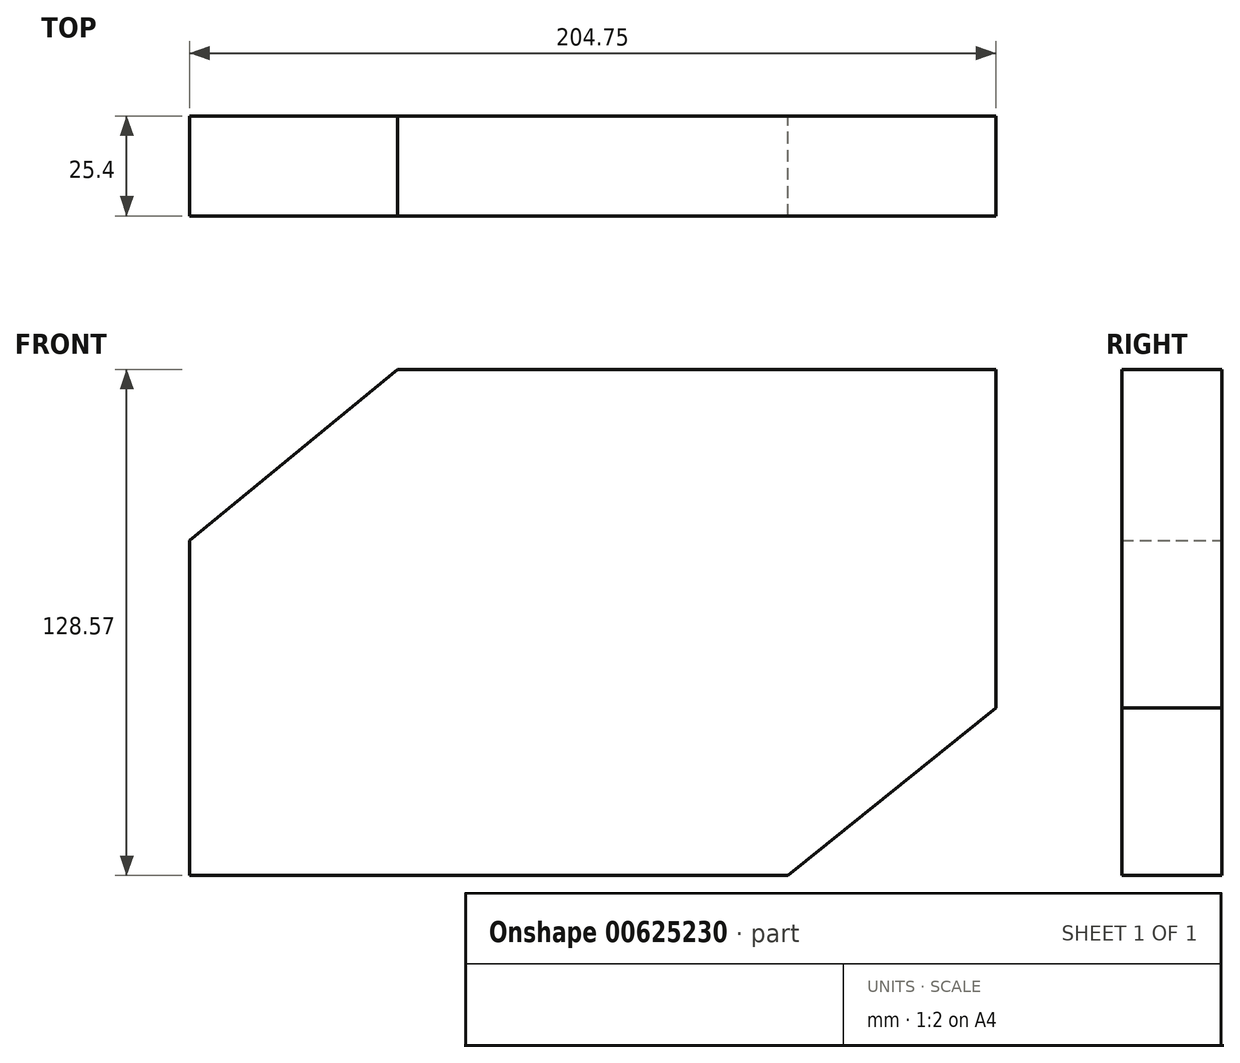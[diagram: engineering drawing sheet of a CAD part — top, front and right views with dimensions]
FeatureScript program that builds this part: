
annotation { "Feature Type Name" : "Feature", "Feature Type Description" : "" }
export const myFeature = defineFeature(function(context is Context, id is Id, definition is map)
    precondition{}
    {
        {
            var Q0;
            Q0=qCreatedBy(makeId("Front.planeOp"),FACE);
            var sketch = newSketch(context, id + "F0", { "sketchPlane" : qUnion([Q0])});
            skLineSegment(sketch, "E0.bottom", {"start": v(76, -42.57) * mm, "end": v(-76, -42.57) * mm});
            skLineSegment(sketch, "E0.top", {"start": v(76, 42.57) * mm, "end": v(-76, 42.57) * mm});
            skLineSegment(sketch, "E0.left", {"start": v(76, -42.57) * mm, "end": v(76, 42.57) * mm});
            skLineSegment(sketch, "E0.right", {"start": v(-76, -42.57) * mm, "end": v(-76, 42.57) * mm});
            skPoint(sketch, "E0.middle", {"position": v(0, 0) * mm});
            skLineSegment(sketch, "E1", {"start": v(76, 42.57) * mm, "end": v(128.75, 86) * mm});
            skLineSegment(sketch, "E2", {"start": v(76, -42.57) * mm, "end": v(128.75, 0) * mm});
            skLineSegment(sketch, "E3", {"start": v(128.75, 86) * mm, "end": v(128.75, 0) * mm});
            skLineSegment(sketch, "E4", {"start": v(128.75, 86) * mm, "end": v(0, 86) * mm});
            skLineSegment(sketch, "E5", {"start": v(-76, 42.57) * mm, "end": v(-23.24, 86) * mm});
            skLineSegment(sketch, "E6", {"start": v(0, 86) * mm, "end": v(-23.24, 86) * mm});
            skLineSegment(sketch, "E7", {"start": v(-76, -42.57) * mm, "end": v(-22.72, 0) * mm});
            skLineSegment(sketch, "E8", {"start": v(-18.54, 0) * mm, "end": v(128.75, 0) * mm});
            skLineSegment(sketch, "E9", {"start": v(-18.54, 0) * mm, "end": v(-23.24, 0) * mm});
            skLineSegment(sketch, "E10", {"start": v(-22.72, 0) * mm, "end": v(-23.24, 86) * mm});
            skSolve(sketch);
        }
        {
            var Q0;
            Q0 = qSketchRegion(id + "F0", true);
            var Q1;
            {var subQ1=sQuery(id+"F0.wireOp",EDGE,"E9");var subQ3=sQuery(id+"F0.wireOp",EDGE,"E8");var subQ4=makeQuery(id+"F0.imprint","INTERSECT",VERTEX,{"derivedFrom":[subQ3,subQ1]});Q1=makeQuery(id+"F0.imprint","IMPRINT",FACE,{"disambiguationData":[TD([[makeQuery(id+"F0.imprint","IMPRINT",EDGE,{"disambiguationData":[TD([[subQ4,-1.0]])],"derivedFrom":subQ3}),1.0]])]});}
            extrude(context, id + "F1", {"entities" : qUnion([Q0, Q1]), "depth" : 25.4 * mm, "offsetDistance" : 25.4 * mm});
        }
    });
